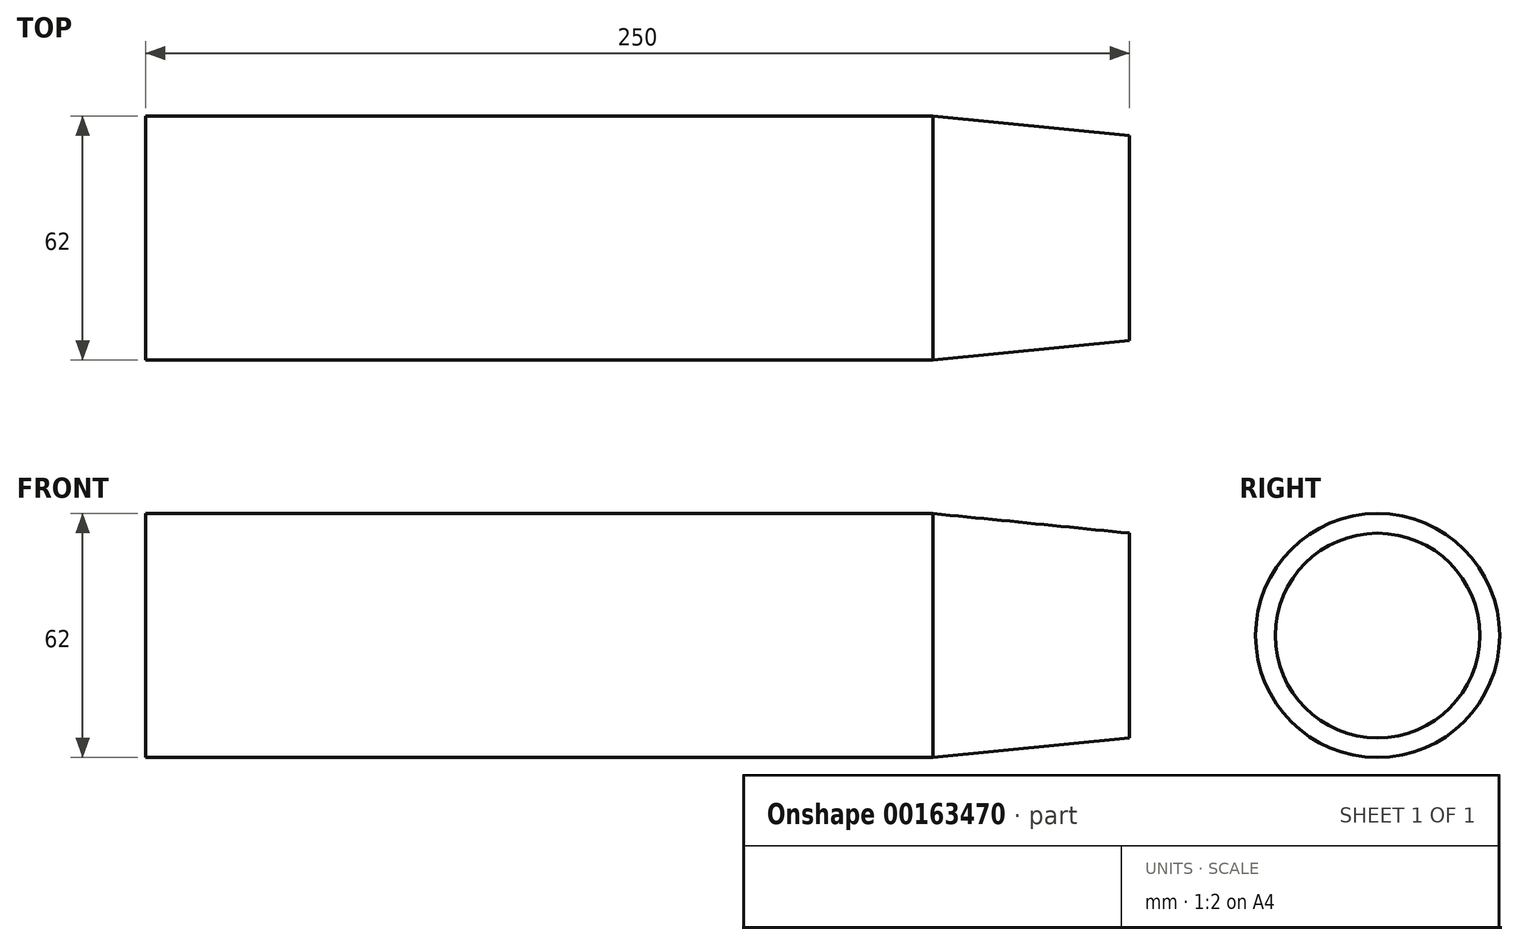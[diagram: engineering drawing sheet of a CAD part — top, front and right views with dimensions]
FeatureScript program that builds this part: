
annotation { "Feature Type Name" : "Feature", "Feature Type Description" : "" }
export const myFeature = defineFeature(function(context is Context, id is Id, definition is map)
    precondition{}
    {
        {
            var Q0;
            Q0=qCreatedBy(makeId("Front.planeOp"),FACE);
            var sketch = newSketch(context, id + "F0", { "sketchPlane" : qUnion([Q0])});
            skLineSegment(sketch, "E0", {"start": v(0, 0) * mm, "end": v(100, 0) * mm});
            skLineSegment(sketch, "E1", {"start": v(0, 0) * mm, "end": v(0, -31) * mm});
            skLineSegment(sketch, "E2", {"start": v(0, -31) * mm, "end": v(150, -31) * mm});
            skLineSegment(sketch, "E3", {"start": v(150, -31) * mm, "end": v(150, -5) * mm});
            skLineSegment(sketch, "E4", {"start": v(150, -5) * mm, "end": v(100, 0) * mm});
            skLineSegment(sketch, "E5", {"start": v(0, 0) * mm, "end": v(-100, 0) * mm});
            skLineSegment(sketch, "E6", {"start": v(-100, 0) * mm, "end": v(-100, -31) * mm});
            skLineSegment(sketch, "E7", {"start": v(-100, -31) * mm, "end": v(0, -31) * mm});
            skSolve(sketch);
        }
        {
            var Q0;
            Q0 = qSketchRegion(id + "F0", true);
            var Q1;
            Q1=sQuery(id+"F0.wireOp",EDGE,"E2");
            revolve(context, id + "F1", {"entities" : qUnion([Q0]), "axis" : qUnion([Q1]), "revolveType" : RevolveType.FULL});
        }
    });
